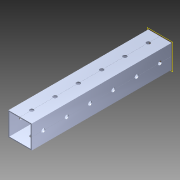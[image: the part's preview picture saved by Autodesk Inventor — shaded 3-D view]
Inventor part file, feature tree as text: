
AUTODESK INVENTOR PART (.ipt)
format: ipt  version: 2014 (Build 180170000, 170)  size: 1,139,712 bytes
history: native  units: in
note: dims shown in document units (in); Inventor stores cm internally (conversion verified against a paired STEP export)
features: pattern_circular x1, other x1, plane x1, extrude x1, imported_body x1, sketch x1
ambient origin geometry x8: Origin, YZ Plane, XZ Plane, XY Plane, X Axis, Y Axis, Z Axis, Center Point
bodies: Body1 (feature_tree)
feature tree (6):
  pattern_circular  "CirPattern2"
  other  "217-3426-STEP1"
  plane  "Work Plane1"
  extrude  "Extrusion1"  Depth=3937.0079in TaperAngle=0.0deg
  imported_body  "Base1"
  sketch  "Sketch1"  dims[d0=-6.0in d1=3937.0079in d2=0.0in]
